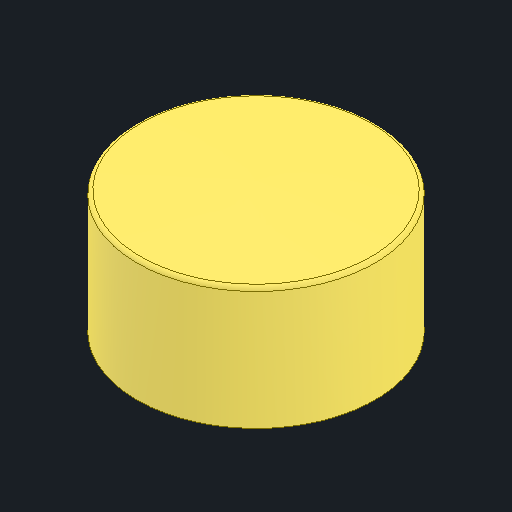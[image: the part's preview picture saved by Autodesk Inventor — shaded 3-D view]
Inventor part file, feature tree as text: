
AUTODESK INVENTOR PART (.ipt)
format: ipt  version: 2024 (Build 280153000, 153)  size: 113,664 bytes
history: native  units: in
note: dims shown in document units (in); Inventor stores cm internally (conversion verified against a paired STEP export)
features: shell x1
ambient origin geometry x8: Origin, YZ Plane, XZ Plane, XY Plane, X Axis, Y Axis, Z Axis, Center Point
bodies: Solid1 (feature_tree)
feature tree (1):
  shell  "Shell1"  [1 undecoded]
note: 1 required parameter value undecoded (feature->parameter linkage not recoverable at this tier; creation-order binding heuristic only, values carry confidence <= 0.55)
